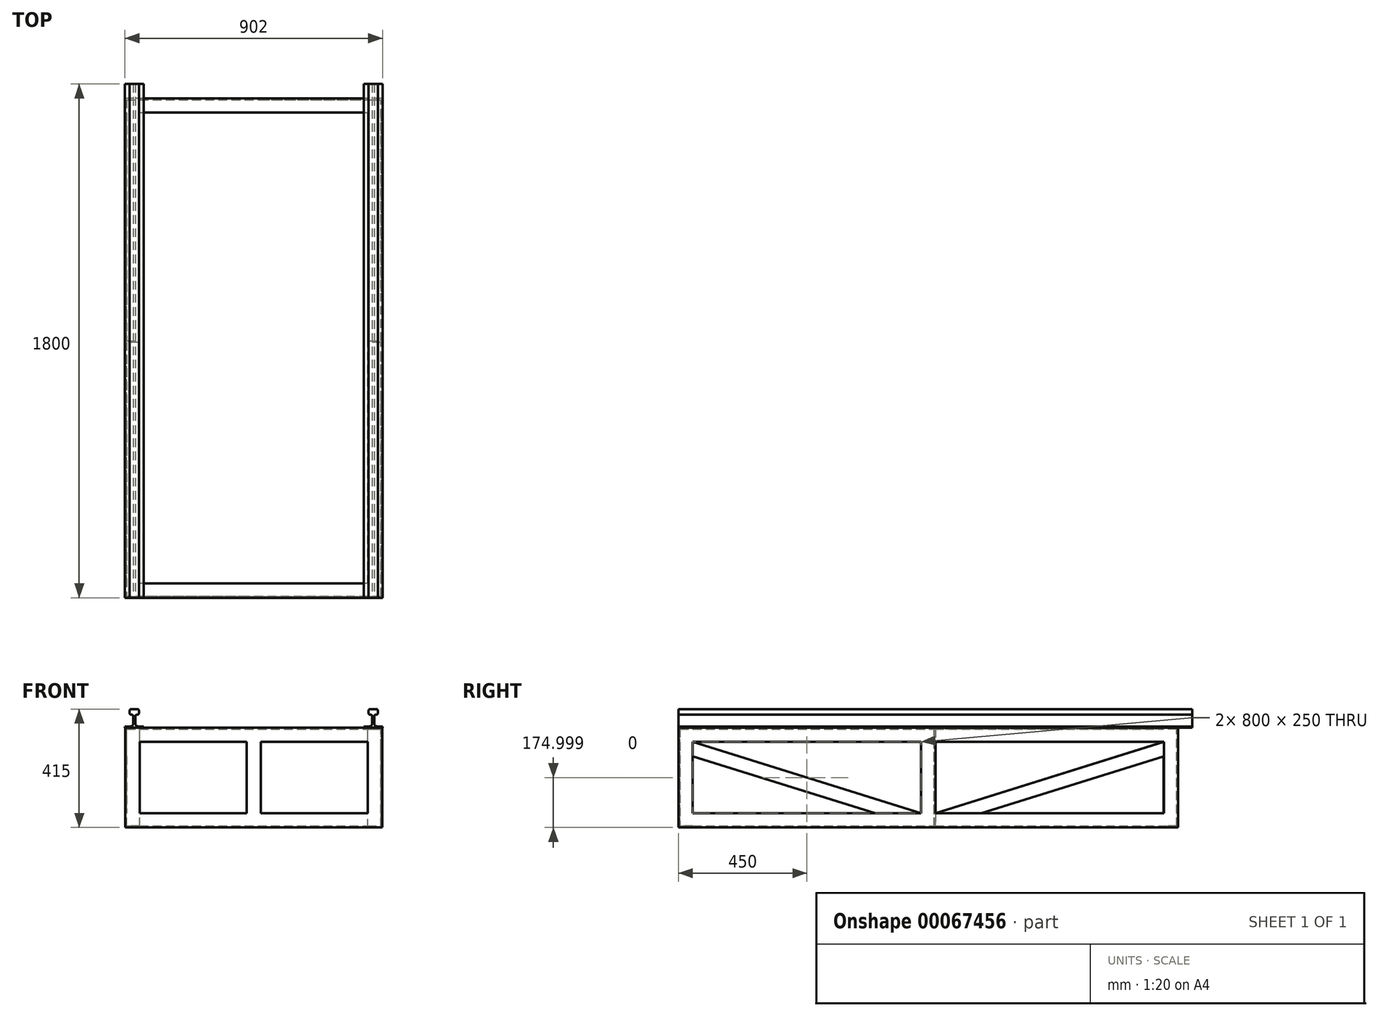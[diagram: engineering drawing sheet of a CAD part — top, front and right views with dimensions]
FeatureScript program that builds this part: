
annotation { "Feature Type Name" : "Feature", "Feature Type Description" : "" }
export const myFeature = defineFeature(function(context is Context, id is Id, definition is map)
    precondition{}
    {
        {
            var Q0;
            Q0=qCreatedBy(makeId("Front.planeOp"),FACE);
            var sketch = newSketch(context, id + "F0", { "sketchPlane" : qUnion([Q0])});
            skLineSegment(sketch, "E0", {"start": v(0, 18.89) * mm, "end": v(0, 13.89) * mm});
            skLineSegment(sketch, "E1", {"start": v(0, 13.89) * mm, "end": v(45, 13.89) * mm});
            skLineSegment(sketch, "E2", {"start": v(45, 13.89) * mm, "end": v(45, -31.11) * mm});
            skLineSegment(sketch, "E3", {"start": v(45, -31.11) * mm, "end": v(50, -31.11) * mm});
            skLineSegment(sketch, "E4", {"start": v(50, -31.11) * mm, "end": v(50, 18.89) * mm});
            skLineSegment(sketch, "E5", {"start": v(50, 18.89) * mm, "end": v(0, 18.89) * mm});
            skSolve(sketch);
        }
        {
            var Q0;
            Q0 = qSketchRegion(id + "F0", true);
            extrude(context, id + "F1", {"entities" : qUnion([Q0]), "depth" : 1750 * mm});
        }
        {
            var Q0;
            Q0=makeQuery(id+"F1.opExtrude","SWEPT_FACE",FACE,{"disambiguationData":[OSD([sQuery(id+"F0.wireOp",EDGE,"E5")])]});
            var sketch = newSketch(context, id + "F2", { "sketchPlane" : qUnion([Q0])});
            skLineSegment(sketch, "E6", {"start": v(45, -5) * mm, "end": v(45, -50) * mm});
            skLineSegment(sketch, "E7", {"start": v(50, -50) * mm, "end": v(50, 0) * mm});
            skLineSegment(sketch, "E8", {"start": v(45, -50) * mm, "end": v(50, -50) * mm});
            skLineSegment(sketch, "E9", {"start": v(0, -5) * mm, "end": v(45, -5) * mm});
            skLineSegment(sketch, "E10", {"start": v(50, 0) * mm, "end": v(0, 0) * mm});
            skLineSegment(sketch, "E11", {"start": v(0, 0) * mm, "end": v(0, -5) * mm});
            skSolve(sketch);
        }
        {
            var Q0;
            Q0 = qSketchRegion(id + "F2", true);
            extrude(context, id + "F3", {"entities" : qUnion([Q0]), "operationType" : NewBodyOperationType.ADD, "oppositeDirection" : true, "depth" : 350 * mm});
        }
        {
            var Q0;
            Q0=makeQuery(id+"F3.boolean.opBoolean","MERGE",FACE,{"derivedFrom":[makeQuery(id+"F1.opExtrude","CAP_FACE",FACE,{"disambiguationData":[OSD([sQuery(id+"F0.wireOp",EDGE,"E0"),sQuery(id+"F0.wireOp",EDGE,"E1"),sQuery(id+"F0.wireOp",EDGE,"E2"),sQuery(id+"F0.wireOp",EDGE,"E3"),sQuery(id+"F0.wireOp",EDGE,"E4"),sQuery(id+"F0.wireOp",EDGE,"E5")])],"isStart":true}),makeQuery(id+"F3.opExtrude","SWEPT_FACE",FACE,{"disambiguationData":[OSD([sQuery(id+"F2.wireOp",EDGE,"E10")])]})]});
            var sketch = newSketch(context, id + "F4", { "sketchPlane" : qUnion([Q0])});
            skLineSegment(sketch, "E12", {"start": v(-50, -331.11) * mm, "end": v(0, -331.11) * mm});
            skLineSegment(sketch, "E13", {"start": v(0, -331.11) * mm, "end": v(-0.05, -326.11) * mm});
            skLineSegment(sketch, "E14", {"start": v(-0.05, -326.11) * mm, "end": v(-45, -326.11) * mm});
            skLineSegment(sketch, "E15", {"start": v(-45, -326.11) * mm, "end": v(-45, -281.11) * mm});
            skLineSegment(sketch, "E16", {"start": v(-45, -281.11) * mm, "end": v(-50, -281.11) * mm});
            skLineSegment(sketch, "E17", {"start": v(-50, -281.11) * mm, "end": v(-50, -331.11) * mm});
            skSolve(sketch);
        }
        {
            var Q0;
            Q0 = qSketchRegion(id + "F4", true);
            extrude(context, id + "F5", {"entities" : qUnion([Q0]), "operationType" : NewBodyOperationType.ADD, "oppositeDirection" : true, "depth" : 1750 * mm});
        }
        {
            var Q0;
            Q0=makeQuery(id+"F5.boolean.opBoolean","MERGE",FACE,{"derivedFrom":[makeQuery(id+"F3.boolean.opBoolean","MERGE",FACE,{"derivedFrom":[makeQuery(id+"F1.opExtrude","SWEPT_FACE",FACE,{"disambiguationData":[OSD([sQuery(id+"F0.wireOp",EDGE,"E4")])]}),makeQuery(id+"F3.opExtrude","SWEPT_FACE",FACE,{"disambiguationData":[OSD([sQuery(id+"F2.wireOp",EDGE,"E7")])]})]}),makeQuery(id+"F5.opExtrude","SWEPT_FACE",FACE,{"disambiguationData":[OSD([sQuery(id+"F4.wireOp",EDGE,"E17")])]})]});
            var sketch = newSketch(context, id + "F6", { "sketchPlane" : qUnion([Q0])});
            skLineSegment(sketch, "E18", {"start": v(-50.08, 18.89) * mm, "end": v(0, 18.89) * mm});
            skLineSegment(sketch, "E19", {"start": v(0, 18.89) * mm, "end": v(0, -31.11) * mm});
            skLineSegment(sketch, "E20", {"start": v(0, -31.11) * mm, "end": v(-5, -31.11) * mm});
            skLineSegment(sketch, "E21", {"start": v(-5, -31.11) * mm, "end": v(-5, 13.89) * mm});
            skLineSegment(sketch, "E22", {"start": v(-5, 13.89) * mm, "end": v(-50.08, 13.89) * mm});
            skLineSegment(sketch, "E23", {"start": v(-50.08, 13.89) * mm, "end": v(-50.08, 18.89) * mm});
            skSolve(sketch);
        }
        {
            var Q0;
            Q0 = qSketchRegion(id + "F6", true);
            extrude(context, id + "F7", {"entities" : qUnion([Q0]), "operationType" : NewBodyOperationType.ADD, "oppositeDirection" : true, "depth" : 900 * mm});
        }
        {
            var Q0;
            Q0=makeQuery(id+"F7.boolean.opBoolean","MERGE",FACE,{"derivedFrom":[makeQuery(id+"F1.opExtrude","SWEPT_FACE",FACE,{"disambiguationData":[OSD([sQuery(id+"F0.wireOp",EDGE,"E5")])]}),makeQuery(id+"F7.opExtrude","SWEPT_FACE",FACE,{"disambiguationData":[OSD([sQuery(id+"F6.wireOp",EDGE,"E18")])]})]});
            var sketch = newSketch(context, id + "F8", { "sketchPlane" : qUnion([Q0])});
            skLineSegment(sketch, "E24", {"start": v(0, -1750) * mm, "end": v(50, -1750) * mm});
            skLineSegment(sketch, "E25", {"start": v(50, -1750) * mm, "end": v(50, -1700) * mm});
            skLineSegment(sketch, "E26", {"start": v(50, -1700) * mm, "end": v(45, -1700) * mm});
            skLineSegment(sketch, "E27", {"start": v(45, -1700) * mm, "end": v(45, -1745) * mm});
            skLineSegment(sketch, "E28", {"start": v(45, -1745) * mm, "end": v(0, -1745) * mm});
            skLineSegment(sketch, "E29", {"start": v(0, -1745) * mm, "end": v(0, -1750) * mm});
            skSolve(sketch);
        }
        {
            var Q0;
            Q0 = qSketchRegion(id + "F8", true);
            extrude(context, id + "F9", {"entities" : qUnion([Q0]), "operationType" : NewBodyOperationType.ADD, "oppositeDirection" : true, "depth" : 350 * mm});
        }
        {
            var Q0;
            Q0=makeQuery(id+"F9.boolean.opBoolean","MERGE",FACE,{"derivedFrom":[makeQuery(id+"F5.boolean.opBoolean","MERGE",FACE,{"derivedFrom":[makeQuery(id+"F3.boolean.opBoolean","MERGE",FACE,{"derivedFrom":[makeQuery(id+"F1.opExtrude","SWEPT_FACE",FACE,{"disambiguationData":[OSD([sQuery(id+"F0.wireOp",EDGE,"E4")])]}),makeQuery(id+"F3.opExtrude","SWEPT_FACE",FACE,{"disambiguationData":[OSD([sQuery(id+"F2.wireOp",EDGE,"E7")])]})]}),makeQuery(id+"F5.opExtrude","SWEPT_FACE",FACE,{"disambiguationData":[OSD([sQuery(id+"F4.wireOp",EDGE,"E17")])]})]}),makeQuery(id+"F9.opExtrude","SWEPT_FACE",FACE,{"disambiguationData":[OSD([sQuery(id+"F8.wireOp",EDGE,"E25")])]})]});
            var sketch = newSketch(context, id + "F10", { "sketchPlane" : qUnion([Q0])});
            skLineSegment(sketch, "E30", {"start": v(0, -331.11) * mm, "end": v(-50, -331.11) * mm});
            skLineSegment(sketch, "E31", {"start": v(-50, -331.11) * mm, "end": v(-50, -326.11) * mm});
            skLineSegment(sketch, "E32", {"start": v(-50, -326.11) * mm, "end": v(-5, -326.11) * mm});
            skLineSegment(sketch, "E33", {"start": v(-5, -326.11) * mm, "end": v(-5, -281.11) * mm});
            skLineSegment(sketch, "E34", {"start": v(-5, -281.11) * mm, "end": v(0, -281.11) * mm});
            skLineSegment(sketch, "E35", {"start": v(0, -281.11) * mm, "end": v(0, -331.11) * mm});
            skSolve(sketch);
        }
        {
            var Q0;
            Q0 = qSketchRegion(id + "F10", true);
            extrude(context, id + "F11", {"entities" : qUnion([Q0]), "operationType" : NewBodyOperationType.ADD, "oppositeDirection" : true, "depth" : 900 * mm});
        }
        {
            var Q0;
            Q0=makeQuery(id+"F7.boolean.opBoolean","MERGE",FACE,{"derivedFrom":[makeQuery(id+"F1.opExtrude","SWEPT_FACE",FACE,{"disambiguationData":[OSD([sQuery(id+"F0.wireOp",EDGE,"E5")])]}),makeQuery(id+"F7.opExtrude","SWEPT_FACE",FACE,{"disambiguationData":[OSD([sQuery(id+"F6.wireOp",EDGE,"E18")])]})]});
            var sketch = newSketch(context, id + "F12", { "sketchPlane" : qUnion([Q0])});
            skLineSegment(sketch, "E36", {"start": v(-850, 0) * mm, "end": v(-800, 0) * mm});
            skLineSegment(sketch, "E37", {"start": v(-800, 0) * mm, "end": v(-800, -5) * mm});
            skLineSegment(sketch, "E38", {"start": v(-800, -5) * mm, "end": v(-845, -5) * mm});
            skLineSegment(sketch, "E39", {"start": v(-845, -5) * mm, "end": v(-845, -50.08) * mm});
            skLineSegment(sketch, "E40", {"start": v(-845, -50.08) * mm, "end": v(-850, -50.08) * mm});
            skLineSegment(sketch, "E41", {"start": v(-850, -50.08) * mm, "end": v(-850, 0) * mm});
            skSolve(sketch);
        }
        {
            var Q0;
            Q0 = qSketchRegion(id + "F12", true);
            extrude(context, id + "F13", {"entities" : qUnion([Q0]), "operationType" : NewBodyOperationType.ADD, "oppositeDirection" : true, "depth" : 350 * mm});
        }
        {
            var Q0;
            Q0=makeQuery(id+"F13.boolean.opBoolean","MERGE",FACE,{"derivedFrom":[makeQuery(id+"F11.boolean.opBoolean","MERGE",FACE,{"derivedFrom":[makeQuery(id+"F7.boolean.opBoolean","MERGE",FACE,{"derivedFrom":[makeQuery(id+"F3.boolean.opBoolean","MERGE",FACE,{"derivedFrom":[makeQuery(id+"F1.opExtrude","CAP_FACE",FACE,{"disambiguationData":[OSD([sQuery(id+"F0.wireOp",EDGE,"E0"),sQuery(id+"F0.wireOp",EDGE,"E1"),sQuery(id+"F0.wireOp",EDGE,"E2"),sQuery(id+"F0.wireOp",EDGE,"E3"),sQuery(id+"F0.wireOp",EDGE,"E4"),sQuery(id+"F0.wireOp",EDGE,"E5")])],"isStart":true}),makeQuery(id+"F3.opExtrude","SWEPT_FACE",FACE,{"disambiguationData":[OSD([sQuery(id+"F2.wireOp",EDGE,"E10")])]})]}),makeQuery(id+"F7.opExtrude","SWEPT_FACE",FACE,{"disambiguationData":[OSD([sQuery(id+"F6.wireOp",EDGE,"E19")])]})]}),makeQuery(id+"F11.opExtrude","SWEPT_FACE",FACE,{"disambiguationData":[OSD([sQuery(id+"F10.wireOp",EDGE,"E35")])]})]}),makeQuery(id+"F13.opExtrude","SWEPT_FACE",FACE,{"disambiguationData":[OSD([sQuery(id+"F12.wireOp",EDGE,"E36")])]})]});
            var sketch = newSketch(context, id + "F14", { "sketchPlane" : qUnion([Q0])});
            skLineSegment(sketch, "E42", {"start": v(850, 18.89) * mm, "end": v(850, -31.11) * mm});
            skLineSegment(sketch, "E43", {"start": v(850, -31.11) * mm, "end": v(845, -31.11) * mm});
            skLineSegment(sketch, "E44", {"start": v(845, -31.11) * mm, "end": v(845, 13.89) * mm});
            skLineSegment(sketch, "E45", {"start": v(845, 13.89) * mm, "end": v(800, 13.89) * mm});
            skLineSegment(sketch, "E46", {"start": v(800, 13.89) * mm, "end": v(800, 18.89) * mm});
            skLineSegment(sketch, "E47", {"start": v(800, 18.89) * mm, "end": v(850, 18.89) * mm});
            skLineSegment(sketch, "E48", {"start": v(850, -331.11) * mm, "end": v(800, -331.11) * mm});
            skLineSegment(sketch, "E49", {"start": v(800, -331.11) * mm, "end": v(800, -326.11) * mm});
            skLineSegment(sketch, "E50", {"start": v(800, -326.11) * mm, "end": v(845, -326.11) * mm});
            skLineSegment(sketch, "E51", {"start": v(845, -326.11) * mm, "end": v(845, -281.11) * mm});
            skLineSegment(sketch, "E52", {"start": v(845, -281.11) * mm, "end": v(850, -281.11) * mm});
            skLineSegment(sketch, "E53", {"start": v(850, -281.11) * mm, "end": v(850, -331.11) * mm});
            skSolve(sketch);
        }
        {
            var Q0;
            Q0 = qSketchRegion(id + "F14", true);
            extrude(context, id + "F15", {"entities" : qUnion([Q0]), "operationType" : NewBodyOperationType.ADD, "oppositeDirection" : true, "depth" : 1750 * mm});
        }
        {
            var Q0;
            Q0=makeQuery(id+"F15.boolean.opBoolean","MERGE",FACE,{"derivedFrom":[makeQuery(id+"F13.boolean.opBoolean","MERGE",FACE,{"derivedFrom":[makeQuery(id+"F7.opExtrude","CAP_FACE",FACE,{"disambiguationData":[OSD([sQuery(id+"F6.wireOp",EDGE,"E18"),sQuery(id+"F6.wireOp",EDGE,"E19"),sQuery(id+"F6.wireOp",EDGE,"E20"),sQuery(id+"F6.wireOp",EDGE,"E21"),sQuery(id+"F6.wireOp",EDGE,"E22"),sQuery(id+"F6.wireOp",EDGE,"E23")])],"isStart":false}),makeQuery(id+"F11.opExtrude","CAP_FACE",FACE,{"disambiguationData":[OSD([sQuery(id+"F10.wireOp",EDGE,"E30"),sQuery(id+"F10.wireOp",EDGE,"E31"),sQuery(id+"F10.wireOp",EDGE,"E32"),sQuery(id+"F10.wireOp",EDGE,"E33"),sQuery(id+"F10.wireOp",EDGE,"E34"),sQuery(id+"F10.wireOp",EDGE,"E35")])],"isStart":false}),makeQuery(id+"F13.opExtrude","SWEPT_FACE",FACE,{"disambiguationData":[OSD([sQuery(id+"F12.wireOp",EDGE,"E41")])]})]}),makeQuery(id+"F15.opExtrude","SWEPT_FACE",FACE,{"disambiguationData":[OSD([sQuery(id+"F14.wireOp",EDGE,"E42")])]}),makeQuery(id+"F15.opExtrude","SWEPT_FACE",FACE,{"disambiguationData":[OSD([sQuery(id+"F14.wireOp",EDGE,"E53")])]})]});
            var sketch = newSketch(context, id + "F16", { "sketchPlane" : qUnion([Q0])});
            skLineSegment(sketch, "E54", {"start": v(1750, 18.89) * mm, "end": v(1700, 18.89) * mm});
            skLineSegment(sketch, "E55", {"start": v(1700, 18.89) * mm, "end": v(1700, 13.89) * mm});
            skLineSegment(sketch, "E56", {"start": v(1700, 13.89) * mm, "end": v(1745, 13.89) * mm});
            skLineSegment(sketch, "E57", {"start": v(1745, 13.89) * mm, "end": v(1745, -31.11) * mm});
            skLineSegment(sketch, "E58", {"start": v(1745, -31.11) * mm, "end": v(1750, -31.11) * mm});
            skLineSegment(sketch, "E59", {"start": v(1750, -31.11) * mm, "end": v(1750, 18.89) * mm});
            skLineSegment(sketch, "E60", {"start": v(1750, -331.11) * mm, "end": v(1750, -281.11) * mm});
            skLineSegment(sketch, "E61", {"start": v(1750, -281.11) * mm, "end": v(1745, -281.11) * mm});
            skLineSegment(sketch, "E62", {"start": v(1745, -281.11) * mm, "end": v(1745, -326.11) * mm});
            skLineSegment(sketch, "E63", {"start": v(1745, -326.11) * mm, "end": v(1700, -326.11) * mm});
            skLineSegment(sketch, "E64", {"start": v(1700, -326.11) * mm, "end": v(1700, -331.11) * mm});
            skLineSegment(sketch, "E65", {"start": v(1700, -331.11) * mm, "end": v(1750, -331.11) * mm});
            skSolve(sketch);
        }
        {
            var Q0;
            Q0 = qSketchRegion(id + "F16", true);
            extrude(context, id + "F17", {"entities" : qUnion([Q0]), "operationType" : NewBodyOperationType.ADD, "oppositeDirection" : true, "depth" : 900 * mm});
        }
        {
            var Q0;
            Q0=makeQuery(id+"F17.boolean.opBoolean","MERGE",FACE,{"derivedFrom":[makeQuery(id+"F15.boolean.opBoolean","MERGE",FACE,{"derivedFrom":[makeQuery(id+"F7.boolean.opBoolean","MERGE",FACE,{"derivedFrom":[makeQuery(id+"F1.opExtrude","SWEPT_FACE",FACE,{"disambiguationData":[OSD([sQuery(id+"F0.wireOp",EDGE,"E5")])]}),makeQuery(id+"F7.opExtrude","SWEPT_FACE",FACE,{"disambiguationData":[OSD([sQuery(id+"F6.wireOp",EDGE,"E18")])]})]}),makeQuery(id+"F15.opExtrude","SWEPT_FACE",FACE,{"disambiguationData":[OSD([sQuery(id+"F14.wireOp",EDGE,"E47")])]})]}),makeQuery(id+"F17.opExtrude","SWEPT_FACE",FACE,{"disambiguationData":[OSD([sQuery(id+"F16.wireOp",EDGE,"E54")])]})]});
            var sketch = newSketch(context, id + "F18", { "sketchPlane" : qUnion([Q0])});
            skLineSegment(sketch, "E66", {"start": v(-850, -1750) * mm, "end": v(-850, -1700) * mm});
            skLineSegment(sketch, "E67", {"start": v(-850, -1700) * mm, "end": v(-845, -1700) * mm});
            skLineSegment(sketch, "E68", {"start": v(-845, -1700) * mm, "end": v(-845, -1745) * mm});
            skLineSegment(sketch, "E69", {"start": v(-845, -1745) * mm, "end": v(-800, -1745) * mm});
            skLineSegment(sketch, "E70", {"start": v(-800, -1745) * mm, "end": v(-800, -1750) * mm});
            skLineSegment(sketch, "E71", {"start": v(-800, -1750) * mm, "end": v(-850, -1750) * mm});
            skSolve(sketch);
        }
        {
            var Q0;
            Q0 = qSketchRegion(id + "F18", true);
            extrude(context, id + "F19", {"entities" : qUnion([Q0]), "operationType" : NewBodyOperationType.ADD, "oppositeDirection" : true, "depth" : 350 * mm});
        }
        {
            var Q0;
            Q0=makeQuery(id+"F17.boolean.opBoolean","MERGE",FACE,{"derivedFrom":[makeQuery(id+"F15.boolean.opBoolean","MERGE",FACE,{"derivedFrom":[makeQuery(id+"F7.boolean.opBoolean","MERGE",FACE,{"derivedFrom":[makeQuery(id+"F1.opExtrude","SWEPT_FACE",FACE,{"disambiguationData":[OSD([sQuery(id+"F0.wireOp",EDGE,"E5")])]}),makeQuery(id+"F7.opExtrude","SWEPT_FACE",FACE,{"disambiguationData":[OSD([sQuery(id+"F6.wireOp",EDGE,"E18")])]})]}),makeQuery(id+"F15.opExtrude","SWEPT_FACE",FACE,{"disambiguationData":[OSD([sQuery(id+"F14.wireOp",EDGE,"E47")])]})]}),makeQuery(id+"F17.opExtrude","SWEPT_FACE",FACE,{"disambiguationData":[OSD([sQuery(id+"F16.wireOp",EDGE,"E54")])]})]});
            var sketch = newSketch(context, id + "F20", { "sketchPlane" : qUnion([Q0])});
            skLineSegment(sketch, "E72", {"start": v(-850, -850) * mm, "end": v(-800, -850) * mm});
            skLineSegment(sketch, "E73", {"start": v(-800, -850) * mm, "end": v(-800, -855) * mm});
            skLineSegment(sketch, "E74", {"start": v(-800, -855) * mm, "end": v(-845, -855) * mm});
            skLineSegment(sketch, "E75", {"start": v(-845, -855) * mm, "end": v(-845, -900) * mm});
            skLineSegment(sketch, "E76", {"start": v(-845, -900) * mm, "end": v(-850, -900) * mm});
            skLineSegment(sketch, "E77", {"start": v(-850, -900) * mm, "end": v(-850, -850) * mm});
            skLineSegment(sketch, "E78", {"start": v(0, -850) * mm, "end": v(50, -850) * mm});
            skLineSegment(sketch, "E79", {"start": v(50, -850) * mm, "end": v(50, -900) * mm});
            skLineSegment(sketch, "E80", {"start": v(50, -900) * mm, "end": v(45, -900) * mm});
            skLineSegment(sketch, "E81", {"start": v(45, -900) * mm, "end": v(45, -855) * mm});
            skLineSegment(sketch, "E82", {"start": v(45, -855) * mm, "end": v(0, -855) * mm});
            skLineSegment(sketch, "E83", {"start": v(0, -855) * mm, "end": v(0, -850) * mm});
            skLineSegment(sketch, "E84.bottom", {"start": v(-425, 0) * mm, "end": v(-375, 0) * mm});
            skLineSegment(sketch, "E84.top", {"start": v(-425, -5) * mm, "end": v(-375, -5) * mm});
            skLineSegment(sketch, "E84.left", {"start": v(-425, 0) * mm, "end": v(-425, -5) * mm});
            skLineSegment(sketch, "E84.right", {"start": v(-375, 0) * mm, "end": v(-375, -5) * mm});
            skLineSegment(sketch, "E85.bottom", {"start": v(-425, -1750) * mm, "end": v(-375, -1750) * mm});
            skLineSegment(sketch, "E85.top", {"start": v(-425, -1745) * mm, "end": v(-375, -1745) * mm});
            skLineSegment(sketch, "E85.left", {"start": v(-425, -1750) * mm, "end": v(-425, -1745) * mm});
            skLineSegment(sketch, "E85.right", {"start": v(-375, -1750) * mm, "end": v(-375, -1745) * mm});
            skSolve(sketch);
        }
        {
            var Q0;
            Q0 = qSketchRegion(id + "F20", true);
            extrude(context, id + "F21", {"entities" : qUnion([Q0]), "operationType" : NewBodyOperationType.ADD, "oppositeDirection" : true, "depth" : 350 * mm});
        }
        {
            var Q0;
            Q0=makeQuery(id+"F21.boolean.opBoolean","MERGE",FACE,{"derivedFrom":[makeQuery(id+"F9.boolean.opBoolean","MERGE",FACE,{"derivedFrom":[makeQuery(id+"F5.boolean.opBoolean","MERGE",FACE,{"derivedFrom":[makeQuery(id+"F3.boolean.opBoolean","MERGE",FACE,{"derivedFrom":[makeQuery(id+"F1.opExtrude","SWEPT_FACE",FACE,{"disambiguationData":[OSD([sQuery(id+"F0.wireOp",EDGE,"E4")])]}),makeQuery(id+"F3.opExtrude","SWEPT_FACE",FACE,{"disambiguationData":[OSD([sQuery(id+"F2.wireOp",EDGE,"E7")])]})]}),makeQuery(id+"F5.opExtrude","SWEPT_FACE",FACE,{"disambiguationData":[OSD([sQuery(id+"F4.wireOp",EDGE,"E17")])]})]}),makeQuery(id+"F9.opExtrude","SWEPT_FACE",FACE,{"disambiguationData":[OSD([sQuery(id+"F8.wireOp",EDGE,"E25")])]})]}),makeQuery(id+"F21.opExtrude","SWEPT_FACE",FACE,{"disambiguationData":[OSD([sQuery(id+"F20.wireOp",EDGE,"E79")])]})]});
            var sketch = newSketch(context, id + "F22", { "sketchPlane" : qUnion([Q0])});
            skLineSegment(sketch, "E86", {"start": v(-850, -281.11) * mm, "end": v(-50, -31.11) * mm});
            skLineSegment(sketch, "E87", {"start": v(-50, -31.11) * mm, "end": v(-50, -81.11) * mm});
            skLineSegment(sketch, "E88", {"start": v(-50, -81.11) * mm, "end": v(-690, -281.11) * mm});
            skLineSegment(sketch, "E89", {"start": v(-690, -281.11) * mm, "end": v(-850, -281.11) * mm});
            skLineSegment(sketch, "E90", {"start": v(-1700, -31.11) * mm, "end": v(-900, -281.11) * mm});
            skLineSegment(sketch, "E91", {"start": v(-900, -281.11) * mm, "end": v(-1060, -281.11) * mm});
            skLineSegment(sketch, "E92", {"start": v(-1060, -281.11) * mm, "end": v(-1700, -81.11) * mm});
            skLineSegment(sketch, "E93", {"start": v(-1700, -81.11) * mm, "end": v(-1700, -31.11) * mm});
            skSolve(sketch);
        }
        {
            var Q0;
            Q0 = qSketchRegion(id + "F22", true);
            extrude(context, id + "F23", {"entities" : qUnion([Q0]), "oppositeDirection" : true, "depth" : 5 * mm});
        }
        {
            var Q0;
            Q0=makeQuery(id+"F21.boolean.opBoolean","MERGE",FACE,{"derivedFrom":[makeQuery(id+"F19.boolean.opBoolean","MERGE",FACE,{"derivedFrom":[makeQuery(id+"F15.boolean.opBoolean","MERGE",FACE,{"derivedFrom":[makeQuery(id+"F13.boolean.opBoolean","MERGE",FACE,{"derivedFrom":[makeQuery(id+"F7.opExtrude","CAP_FACE",FACE,{"disambiguationData":[OSD([sQuery(id+"F6.wireOp",EDGE,"E18"),sQuery(id+"F6.wireOp",EDGE,"E19"),sQuery(id+"F6.wireOp",EDGE,"E20"),sQuery(id+"F6.wireOp",EDGE,"E21"),sQuery(id+"F6.wireOp",EDGE,"E22"),sQuery(id+"F6.wireOp",EDGE,"E23")])],"isStart":false}),makeQuery(id+"F11.opExtrude","CAP_FACE",FACE,{"disambiguationData":[OSD([sQuery(id+"F10.wireOp",EDGE,"E30"),sQuery(id+"F10.wireOp",EDGE,"E31"),sQuery(id+"F10.wireOp",EDGE,"E32"),sQuery(id+"F10.wireOp",EDGE,"E33"),sQuery(id+"F10.wireOp",EDGE,"E34"),sQuery(id+"F10.wireOp",EDGE,"E35")])],"isStart":false}),makeQuery(id+"F13.opExtrude","SWEPT_FACE",FACE,{"disambiguationData":[OSD([sQuery(id+"F12.wireOp",EDGE,"E41")])]})]}),makeQuery(id+"F15.opExtrude","SWEPT_FACE",FACE,{"disambiguationData":[OSD([sQuery(id+"F14.wireOp",EDGE,"E42")])]}),makeQuery(id+"F15.opExtrude","SWEPT_FACE",FACE,{"disambiguationData":[OSD([sQuery(id+"F14.wireOp",EDGE,"E53")])]})]}),makeQuery(id+"F19.opExtrude","SWEPT_FACE",FACE,{"disambiguationData":[OSD([sQuery(id+"F18.wireOp",EDGE,"E66")])]})]}),makeQuery(id+"F21.opExtrude","SWEPT_FACE",FACE,{"disambiguationData":[OSD([sQuery(id+"F20.wireOp",EDGE,"E77")])]})]});
            var sketch = newSketch(context, id + "F24", { "sketchPlane" : qUnion([Q0])});
            skLineSegment(sketch, "E94", {"start": v(50.08, -31.11) * mm, "end": v(850, -281.11) * mm});
            skLineSegment(sketch, "E95", {"start": v(850, -281.11) * mm, "end": v(690.02, -281.11) * mm});
            skLineSegment(sketch, "E96", {"start": v(690.02, -281.11) * mm, "end": v(50.08, -81.11) * mm});
            skLineSegment(sketch, "E97", {"start": v(50.08, -81.11) * mm, "end": v(50.08, -31.11) * mm});
            skLineSegment(sketch, "E98", {"start": v(900, -281.11) * mm, "end": v(1700, -31.11) * mm});
            skLineSegment(sketch, "E99", {"start": v(1700, -31.11) * mm, "end": v(1700, -81.11) * mm});
            skLineSegment(sketch, "E100", {"start": v(1700, -81.11) * mm, "end": v(1060, -281.11) * mm});
            skLineSegment(sketch, "E101", {"start": v(1060, -281.11) * mm, "end": v(900, -281.11) * mm});
            skSolve(sketch);
        }
        {
            var Q0;
            Q0 = qSketchRegion(id + "F24", true);
            extrude(context, id + "F25", {"entities" : qUnion([Q0]), "oppositeDirection" : true, "depth" : 5 * mm});
        }
        {
            var Q0;
            Q0=makeQuery(id+"F21.boolean.opBoolean","MERGE",FACE,{"derivedFrom":[makeQuery(id+"F19.boolean.opBoolean","MERGE",FACE,{"derivedFrom":[makeQuery(id+"F17.boolean.opBoolean","MERGE",FACE,{"derivedFrom":[makeQuery(id+"F9.boolean.opBoolean","MERGE",FACE,{"derivedFrom":[makeQuery(id+"F1.opExtrude","CAP_FACE",FACE,{"disambiguationData":[OSD([sQuery(id+"F0.wireOp",EDGE,"E0"),sQuery(id+"F0.wireOp",EDGE,"E1"),sQuery(id+"F0.wireOp",EDGE,"E2"),sQuery(id+"F0.wireOp",EDGE,"E3"),sQuery(id+"F0.wireOp",EDGE,"E4"),sQuery(id+"F0.wireOp",EDGE,"E5")])],"isStart":false}),makeQuery(id+"F5.opExtrude","CAP_FACE",FACE,{"disambiguationData":[OSD([sQuery(id+"F4.wireOp",EDGE,"E12"),sQuery(id+"F4.wireOp",EDGE,"E13"),sQuery(id+"F4.wireOp",EDGE,"E14"),sQuery(id+"F4.wireOp",EDGE,"E15"),sQuery(id+"F4.wireOp",EDGE,"E16"),sQuery(id+"F4.wireOp",EDGE,"E17")])],"isStart":false}),makeQuery(id+"F9.opExtrude","SWEPT_FACE",FACE,{"disambiguationData":[OSD([sQuery(id+"F8.wireOp",EDGE,"E24")])]})]}),makeQuery(id+"F15.opExtrude","CAP_FACE",FACE,{"disambiguationData":[OSD([sQuery(id+"F14.wireOp",EDGE,"E42"),sQuery(id+"F14.wireOp",EDGE,"E43"),sQuery(id+"F14.wireOp",EDGE,"E44"),sQuery(id+"F14.wireOp",EDGE,"E45"),sQuery(id+"F14.wireOp",EDGE,"E46"),sQuery(id+"F14.wireOp",EDGE,"E47")])],"isStart":false}),makeQuery(id+"F15.opExtrude","CAP_FACE",FACE,{"disambiguationData":[OSD([sQuery(id+"F14.wireOp",EDGE,"E48"),sQuery(id+"F14.wireOp",EDGE,"E49"),sQuery(id+"F14.wireOp",EDGE,"E50"),sQuery(id+"F14.wireOp",EDGE,"E51"),sQuery(id+"F14.wireOp",EDGE,"E52"),sQuery(id+"F14.wireOp",EDGE,"E53")])],"isStart":false}),makeQuery(id+"F17.opExtrude","SWEPT_FACE",FACE,{"disambiguationData":[OSD([sQuery(id+"F16.wireOp",EDGE,"E59")])]}),makeQuery(id+"F17.opExtrude","SWEPT_FACE",FACE,{"disambiguationData":[OSD([sQuery(id+"F16.wireOp",EDGE,"E60")])]})]}),makeQuery(id+"F19.opExtrude","SWEPT_FACE",FACE,{"disambiguationData":[OSD([sQuery(id+"F18.wireOp",EDGE,"E71")])]})]}),makeQuery(id+"F21.opExtrude","SWEPT_FACE",FACE,{"disambiguationData":[OSD([sQuery(id+"F20.wireOp",EDGE,"E85.bottom")])]})]});
            var sketch = newSketch(context, id + "F26", { "sketchPlane" : qUnion([Q0])});
            skLineSegment(sketch, "E102", {"start": v(-14, 18.89) * mm, "end": v(51, 18.89) * mm});
            skLineSegment(sketch, "E103", {"start": v(51, 18.89) * mm, "end": v(51, 21.89) * mm});
            skLineSegment(sketch, "E104", {"start": v(51, 21.89) * mm, "end": v(31.31, 23.25) * mm});
            skLineSegment(sketch, "E105", {"start": v(22, 33.22) * mm, "end": v(22, 58.89) * mm});
            skLineSegment(sketch, "E106", {"start": v(27, 63.89) * mm, "end": v(29.5, 63.89) * mm});
            skLineSegment(sketch, "E107", {"start": v(34.5, 68.89) * mm, "end": v(34.5, 78.89) * mm});
            skLineSegment(sketch, "E108", {"start": v(29.5, 83.89) * mm, "end": v(7.5, 83.89) * mm});
            skLineSegment(sketch, "E109", {"start": v(2.5, 78.89) * mm, "end": v(2.5, 68.89) * mm});
            skLineSegment(sketch, "E110", {"start": v(7.5, 63.89) * mm, "end": v(10, 63.89) * mm});
            skLineSegment(sketch, "E111", {"start": v(15, 58.89) * mm, "end": v(15, 33.22) * mm});
            skLineSegment(sketch, "E112", {"start": v(-14, 18.89) * mm, "end": v(-14, 21.89) * mm});
            skLineSegment(sketch, "E113", {"start": v(-14, 21.89) * mm, "end": v(5.69, 23.25) * mm});
            skPoint(sketch, "E114.visualSharp", {"position": v(34.5, 83.89) * mm});
            skArc(sketch, "E114.filletArc", {"start": v(34.5, 78.89) * mm, "mid": v(33.04, 82.42) * mm, "end": v(29.5, 83.89) * mm});
            skPoint(sketch, "E115.visualSharp", {"position": v(2.5, 83.89) * mm});
            skArc(sketch, "E115.filletArc", {"start": v(7.5, 83.89) * mm, "mid": v(3.96, 82.42) * mm, "end": v(2.5, 78.89) * mm});
            skPoint(sketch, "E116.visualSharp", {"position": v(2.5, 63.89) * mm});
            skArc(sketch, "E116.filletArc", {"start": v(2.5, 68.89) * mm, "mid": v(3.96, 65.35) * mm, "end": v(7.5, 63.89) * mm});
            skPoint(sketch, "E117.visualSharp", {"position": v(34.5, 63.89) * mm});
            skArc(sketch, "E117.filletArc", {"start": v(29.5, 63.89) * mm, "mid": v(33.04, 65.35) * mm, "end": v(34.5, 68.89) * mm});
            skPoint(sketch, "E118.visualSharp", {"position": v(22, 63.89) * mm});
            skArc(sketch, "E118.filletArc", {"start": v(27, 63.89) * mm, "mid": v(23.46, 62.42) * mm, "end": v(22, 58.89) * mm});
            skPoint(sketch, "E119.visualSharp", {"position": v(15, 63.89) * mm});
            skArc(sketch, "E119.filletArc", {"start": v(15, 58.89) * mm, "mid": v(13.54, 62.42) * mm, "end": v(10, 63.89) * mm});
            skPoint(sketch, "E120.visualSharp", {"position": v(22, 23.89) * mm});
            skArc(sketch, "E120.filletArc", {"start": v(22, 33.22) * mm, "mid": v(24.69, 26.4) * mm, "end": v(31.31, 23.25) * mm});
            skPoint(sketch, "E121.visualSharp", {"position": v(15, 23.89) * mm});
            skArc(sketch, "E121.filletArc", {"start": v(5.69, 23.25) * mm, "mid": v(12.31, 26.4) * mm, "end": v(15, 33.22) * mm});
            skPoint(sketch, "E122.visualSharp", {"position": v(-802.5, 83.89) * mm});
            skLineSegment(sketch, "E123", {"start": v(-851, 21.89) * mm, "end": v(-831.31, 23.25) * mm});
            skLineSegment(sketch, "E124", {"start": v(-822, 58.89) * mm, "end": v(-822, 33.22) * mm});
            skLineSegment(sketch, "E125", {"start": v(-815, 33.22) * mm, "end": v(-815, 58.89) * mm});
            skLineSegment(sketch, "E126", {"start": v(-786, 21.89) * mm, "end": v(-805.69, 23.25) * mm});
            skLineSegment(sketch, "E127", {"start": v(-851, 18.89) * mm, "end": v(-786, 18.89) * mm});
            skPoint(sketch, "E128.visualSharp", {"position": v(-822, 23.89) * mm});
            skPoint(sketch, "E129.visualSharp", {"position": v(-834.5, 83.89) * mm});
            skPoint(sketch, "E130.visualSharp", {"position": v(-815, 23.89) * mm});
            skPoint(sketch, "E131.visualSharp", {"position": v(-815, 63.89) * mm});
            skPoint(sketch, "E132.visualSharp", {"position": v(-822, 63.89) * mm});
            skPoint(sketch, "E133.visualSharp", {"position": v(-802.5, 63.89) * mm});
            skLineSegment(sketch, "E134", {"start": v(-807.5, 83.89) * mm, "end": v(-829.5, 83.89) * mm});
            skPoint(sketch, "E135.visualSharp", {"position": v(-834.5, 63.89) * mm});
            skLineSegment(sketch, "E136", {"start": v(-851, 18.89) * mm, "end": v(-851, 21.89) * mm});
            skArc(sketch, "E130.filletArc", {"start": v(-815, 33.22) * mm, "mid": v(-812.31, 26.4) * mm, "end": v(-805.69, 23.25) * mm});
            skLineSegment(sketch, "E137", {"start": v(-786, 18.89) * mm, "end": v(-786, 21.89) * mm});
            skArc(sketch, "E128.filletArc", {"start": v(-831.31, 23.25) * mm, "mid": v(-824.69, 26.4) * mm, "end": v(-822, 33.22) * mm});
            skArc(sketch, "E122.filletArc", {"start": v(-802.5, 78.89) * mm, "mid": v(-803.96, 82.42) * mm, "end": v(-807.5, 83.89) * mm});
            skLineSegment(sketch, "E138", {"start": v(-802.5, 68.89) * mm, "end": v(-802.5, 78.89) * mm});
            skLineSegment(sketch, "E139", {"start": v(-834.5, 78.89) * mm, "end": v(-834.5, 68.89) * mm});
            skArc(sketch, "E129.filletArc", {"start": v(-829.5, 83.89) * mm, "mid": v(-833.04, 82.42) * mm, "end": v(-834.5, 78.89) * mm});
            skLineSegment(sketch, "E140", {"start": v(-810, 63.89) * mm, "end": v(-807.5, 63.89) * mm});
            skArc(sketch, "E132.filletArc", {"start": v(-822, 58.89) * mm, "mid": v(-823.46, 62.42) * mm, "end": v(-827, 63.89) * mm});
            skLineSegment(sketch, "E141", {"start": v(-829.5, 63.89) * mm, "end": v(-827, 63.89) * mm});
            skArc(sketch, "E133.filletArc", {"start": v(-807.5, 63.89) * mm, "mid": v(-803.96, 65.35) * mm, "end": v(-802.5, 68.89) * mm});
            skArc(sketch, "E135.filletArc", {"start": v(-834.5, 68.89) * mm, "mid": v(-833.04, 65.35) * mm, "end": v(-829.5, 63.89) * mm});
            skArc(sketch, "E131.filletArc", {"start": v(-810, 63.89) * mm, "mid": v(-813.54, 62.42) * mm, "end": v(-815, 58.89) * mm});
            skSolve(sketch);
        }
        {
            var Q0;
            Q0 = qSketchRegion(id + "F26", true);
            extrude(context, id + "F27", {"entities" : qUnion([Q0]), "oppositeDirection" : true, "depth" : (1750 + 50) * mm});
        }
    });
